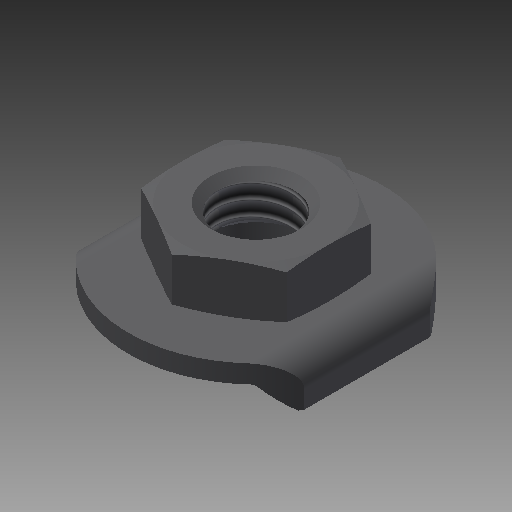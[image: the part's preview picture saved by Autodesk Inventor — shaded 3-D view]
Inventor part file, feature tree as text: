
AUTODESK INVENTOR PART (.ipt)
format: ipt  version: 2018 (Build 220112000, 112)  size: 188,928 bytes
history: native  units: mm
features: other x14, sketch x5, extrude x3, revolve x2, thread x1
ambient origin geometry x8: Origin, YZ Plane, XZ Plane, XY Plane, X Axis, Y Axis, Z Axis, Center Point
bodies: Solid1 (feature_tree)
feature tree (25):
  extrude  "Extrusion1"  TaperAngle=360.0deg  [1 undecoded]
  revolve  "Revolution1"  [1 undecoded]
  extrude  "Extrusion2"  Depth=1.834mm TaperAngle=0.0deg
  extrude  "Extrusion3"  [1 undecoded]
  revolve  "Revolution2"  [1 undecoded]
  thread  "Thread1"  [1 undecoded]
  other  "FS1_XY"
  other  "FS1_YZ"
  other  "FS1_ZX"
  other  "FS1_X"
  other  "FS1_Y"
  other  "FS1_Z"
  other  "FS1_Center"
  other  "FS2_XY"
  other  "FS2_YZ"
  other  "FS2_ZX"
  other  "FS2_X"
  other  "FS2_Y"
  other  "FS2_Z"
  other  "FS2_Center"
  sketch  "Skizze_1"  dims[d0=14.0mm d1=0.0mm d2=360.0deg]
  sketch  "Skizze_2"  dims[d7=360.0deg d8=1.834mm d9=0.0mm]
  sketch  "Skizze_3"
  sketch  "Skizze_4"
  sketch  "Skizze_5_ALT_Drilling_1"  dims[d3=2.7mm d4=0.0mm d5=10.0mm d6=0.0mm]
note: 5 required parameter values undecoded (feature->parameter linkage not recoverable at this tier; creation-order binding heuristic only, values carry confidence <= 0.55)